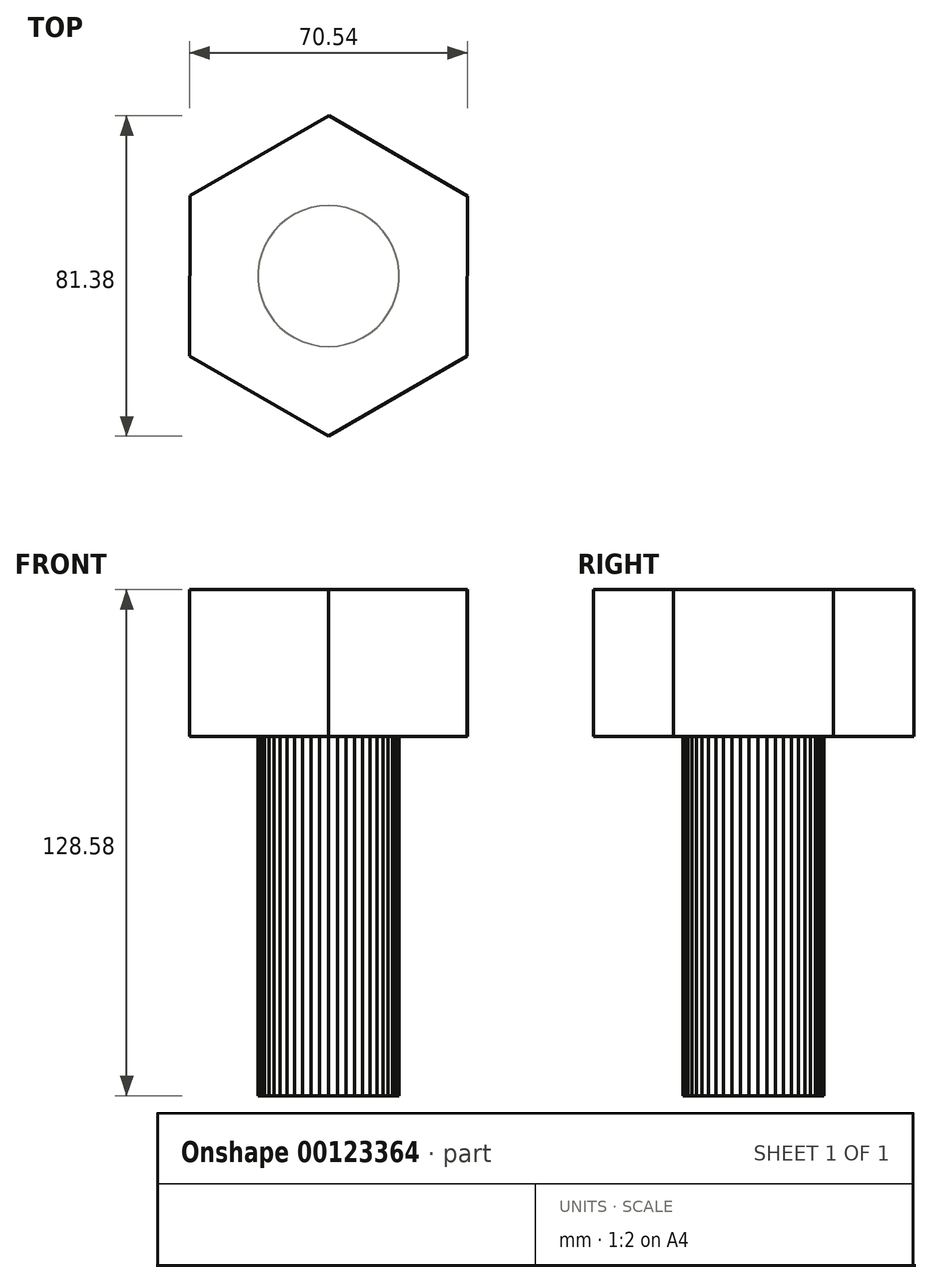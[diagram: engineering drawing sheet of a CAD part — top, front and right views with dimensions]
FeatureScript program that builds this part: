
annotation { "Feature Type Name" : "Feature", "Feature Type Description" : "" }
export const myFeature = defineFeature(function(context is Context, id is Id, definition is map)
    precondition{}
    {
        {
            var Q0;
            Q0=qCreatedBy(makeId("Top.planeOp"),FACE);
            var sketch = newSketch(context, id + "F0", { "sketchPlane" : qUnion([Q0])});
            skCircle(sketch, "E0.cCircle", {"center": v(0, 0) * mm, "radius": 35.24 * mm, "construction": true});
            skLineSegment(sketch, "E0.0", {"start": v(-35.22, 20.4) * mm, "end": v(0.05, 40.7) * mm});
            skLineSegment(sketch, "E0.1", {"start": v(0.05, 40.7) * mm, "end": v(35.27, 20.3) * mm});
            skLineSegment(sketch, "E0.2", {"start": v(35.27, 20.3) * mm, "end": v(35.22, -20.4) * mm});
            skLineSegment(sketch, "E0.3", {"start": v(35.22, -20.4) * mm, "end": v(-0.05, -40.7) * mm});
            skLineSegment(sketch, "E0.4", {"start": v(-0.05, -40.7) * mm, "end": v(-35.27, -20.3) * mm});
            skLineSegment(sketch, "E0.5", {"start": v(-35.27, -20.3) * mm, "end": v(-35.22, 20.4) * mm});
            skPoint(sketch, "E0.0.midPoint", {"position": v(-17.58, 30.54) * mm});
            skSolve(sketch);
        }
        {
            var Q0;
            Q0 = qSketchRegion(id + "F0", true);
            extrude(context, id + "F1", {"entities" : qUnion([Q0]), "depth" : 37.32 * mm});
        }
        {
            var Q0;
            Q0=makeQuery(id+"F1.opExtrude","CAP_FACE",FACE,{"disambiguationData":[OSD([sQuery(id+"F0.wireOp",EDGE,"E0.0"),sQuery(id+"F0.wireOp",EDGE,"E0.1"),sQuery(id+"F0.wireOp",EDGE,"E0.2"),sQuery(id+"F0.wireOp",EDGE,"E0.3"),sQuery(id+"F0.wireOp",EDGE,"E0.4"),sQuery(id+"F0.wireOp",EDGE,"E0.5")])],"isStart":true});
            var sketch = newSketch(context, id + "F2", { "sketchPlane" : qUnion([Q0])});
            skCircle(sketch, "E1.cCircle", {"center": v(0, 0) * mm, "radius": 17.88 * mm, "construction": true});
            skLineSegment(sketch, "E1.0", {"start": v(-17.88, -1.12) * mm, "end": v(-17.88, 1.12) * mm});
            skLineSegment(sketch, "E1.1", {"start": v(-17.88, 1.12) * mm, "end": v(-17.6, 3.36) * mm});
            skLineSegment(sketch, "E1.2", {"start": v(-17.6, 3.36) * mm, "end": v(-17.04, 5.54) * mm});
            skLineSegment(sketch, "E1.3", {"start": v(-17.04, 5.54) * mm, "end": v(-16.2, 7.63) * mm});
            skLineSegment(sketch, "E1.4", {"start": v(-16.2, 7.63) * mm, "end": v(-15.13, 9.6) * mm});
            skLineSegment(sketch, "E1.5", {"start": v(-15.13, 9.6) * mm, "end": v(-13.8, 11.42) * mm});
            skLineSegment(sketch, "E1.6", {"start": v(-13.8, 11.42) * mm, "end": v(-12.26, 13.06) * mm});
            skLineSegment(sketch, "E1.7", {"start": v(-12.26, 13.06) * mm, "end": v(-10.53, 14.5) * mm});
            skLineSegment(sketch, "E1.8", {"start": v(-10.53, 14.5) * mm, "end": v(-8.63, 15.7) * mm});
            skLineSegment(sketch, "E1.9", {"start": v(-8.63, 15.7) * mm, "end": v(-6.6, 16.66) * mm});
            skLineSegment(sketch, "E1.10", {"start": v(-6.6, 16.66) * mm, "end": v(-4.46, 17.35) * mm});
            skLineSegment(sketch, "E1.11", {"start": v(-4.46, 17.35) * mm, "end": v(-2.25, 17.77) * mm});
            skLineSegment(sketch, "E1.12", {"start": v(-2.25, 17.77) * mm, "end": v(0, 17.91) * mm});
            skLineSegment(sketch, "E1.13", {"start": v(0, 17.91) * mm, "end": v(2.25, 17.77) * mm});
            skLineSegment(sketch, "E1.14", {"start": v(2.25, 17.77) * mm, "end": v(4.46, 17.35) * mm});
            skLineSegment(sketch, "E1.15", {"start": v(4.46, 17.35) * mm, "end": v(6.6, 16.66) * mm});
            skLineSegment(sketch, "E1.16", {"start": v(6.6, 16.66) * mm, "end": v(8.63, 15.7) * mm});
            skLineSegment(sketch, "E1.17", {"start": v(8.63, 15.7) * mm, "end": v(10.53, 14.5) * mm});
            skLineSegment(sketch, "E1.18", {"start": v(10.53, 14.5) * mm, "end": v(12.26, 13.06) * mm});
            skLineSegment(sketch, "E1.19", {"start": v(12.26, 13.06) * mm, "end": v(13.8, 11.42) * mm});
            skLineSegment(sketch, "E1.20", {"start": v(13.8, 11.42) * mm, "end": v(15.13, 9.6) * mm});
            skLineSegment(sketch, "E1.21", {"start": v(15.13, 9.6) * mm, "end": v(16.2, 7.63) * mm});
            skLineSegment(sketch, "E1.22", {"start": v(16.2, 7.63) * mm, "end": v(17.04, 5.54) * mm});
            skLineSegment(sketch, "E1.23", {"start": v(17.04, 5.54) * mm, "end": v(17.6, 3.36) * mm});
            skLineSegment(sketch, "E1.24", {"start": v(17.6, 3.36) * mm, "end": v(17.88, 1.12) * mm});
            skLineSegment(sketch, "E1.25", {"start": v(17.88, 1.12) * mm, "end": v(17.88, -1.12) * mm});
            skLineSegment(sketch, "E1.26", {"start": v(17.88, -1.12) * mm, "end": v(17.6, -3.36) * mm});
            skLineSegment(sketch, "E1.27", {"start": v(17.6, -3.36) * mm, "end": v(17.04, -5.54) * mm});
            skLineSegment(sketch, "E1.28", {"start": v(17.04, -5.54) * mm, "end": v(16.2, -7.63) * mm});
            skLineSegment(sketch, "E1.29", {"start": v(16.2, -7.63) * mm, "end": v(15.13, -9.6) * mm});
            skLineSegment(sketch, "E1.30", {"start": v(15.13, -9.6) * mm, "end": v(13.8, -11.42) * mm});
            skLineSegment(sketch, "E1.31", {"start": v(13.8, -11.42) * mm, "end": v(12.26, -13.06) * mm});
            skLineSegment(sketch, "E1.32", {"start": v(12.26, -13.06) * mm, "end": v(10.53, -14.5) * mm});
            skLineSegment(sketch, "E1.33", {"start": v(10.53, -14.5) * mm, "end": v(8.63, -15.7) * mm});
            skLineSegment(sketch, "E1.34", {"start": v(8.63, -15.7) * mm, "end": v(6.6, -16.66) * mm});
            skLineSegment(sketch, "E1.35", {"start": v(6.6, -16.66) * mm, "end": v(4.46, -17.35) * mm});
            skLineSegment(sketch, "E1.36", {"start": v(4.46, -17.35) * mm, "end": v(2.25, -17.77) * mm});
            skLineSegment(sketch, "E1.37", {"start": v(2.25, -17.77) * mm, "end": v(0, -17.91) * mm});
            skLineSegment(sketch, "E1.38", {"start": v(0, -17.91) * mm, "end": v(-2.25, -17.77) * mm});
            skLineSegment(sketch, "E1.39", {"start": v(-2.25, -17.77) * mm, "end": v(-4.46, -17.35) * mm});
            skLineSegment(sketch, "E1.40", {"start": v(-4.46, -17.35) * mm, "end": v(-6.6, -16.66) * mm});
            skLineSegment(sketch, "E1.41", {"start": v(-6.6, -16.66) * mm, "end": v(-8.63, -15.7) * mm});
            skLineSegment(sketch, "E1.42", {"start": v(-8.63, -15.7) * mm, "end": v(-10.53, -14.5) * mm});
            skLineSegment(sketch, "E1.43", {"start": v(-10.53, -14.5) * mm, "end": v(-12.26, -13.06) * mm});
            skLineSegment(sketch, "E1.44", {"start": v(-12.26, -13.06) * mm, "end": v(-13.8, -11.42) * mm});
            skLineSegment(sketch, "E1.45", {"start": v(-13.8, -11.42) * mm, "end": v(-15.13, -9.6) * mm});
            skLineSegment(sketch, "E1.46", {"start": v(-15.13, -9.6) * mm, "end": v(-16.2, -7.63) * mm});
            skLineSegment(sketch, "E1.47", {"start": v(-16.2, -7.63) * mm, "end": v(-17.04, -5.54) * mm});
            skLineSegment(sketch, "E1.48", {"start": v(-17.04, -5.54) * mm, "end": v(-17.6, -3.36) * mm});
            skLineSegment(sketch, "E1.49", {"start": v(-17.6, -3.36) * mm, "end": v(-17.88, -1.12) * mm});
            skPoint(sketch, "E1.0.midPoint", {"position": v(-17.88, 0) * mm});
            skSolve(sketch);
        }
        {
            var Q0;
            Q0 = qSketchRegion(id + "F2", true);
            extrude(context, id + "F3", {"entities" : qUnion([Q0]), "operationType" : NewBodyOperationType.ADD, "depth" : 91.26 * mm});
        }
    });
